# Revit family: шаблон семейства 2017
name_source: partatom
category: Электрооборудование
revit_build: Autodesk Revit 2017 (Build: 20170118_1100(x64)
units: mm (PartAtom-declared; Revit-internal decimal feet)

## family parameters
Всегда вертикально = Да
Конфигурация панели = Два столбца, слева направо
На основе рабочей плоскости = Да
Общий = Нет
При загрузке вырезать с полостями = Нет
Размер круглого соединителя = Использовать диаметр
Тип детали = Щит
Точка расчета площади = Нет

## types (1)
- STS-4951
    ADSK_URL страницы изделия = https://stilsoft.ru
    ADSK_Единица измерения = шт.
    ADSK_Завод-изготовитель = ООО «Основа Безопасности»
    ADSK_Количество = 1
    ADSK_Марка = СТВФ.426471.042
    ADSK_Масса = 0.07
    ADSK_Наименование = Сплиттер РоЕ STS-4951
    ADSK_Размер_Высота = 28 мм
    ADSK_Размер_Глубина = 66 мм
    ADSK_Размер_Длина = 66 мм
    d_короба = 0 мм
    Время непрерывной работы = круглосуточно
    Входное напряжение постоянного тока (РоЕ), В = 6…28
    Выходной ток, не более, А = 2 А
    Диапазон рабочих температур, °С = от – 40 до + 50
    Количество разъемов PoE / LAN / электропитания, шт = 1 / 1 / 1
    Напряжение = 5
    Отметка по умолчанию = 1219 мм
    Расстояние передачи, до, м = 100 мм
    Стандарт интерфейса связи = 10/100 Base-T Ethernet
